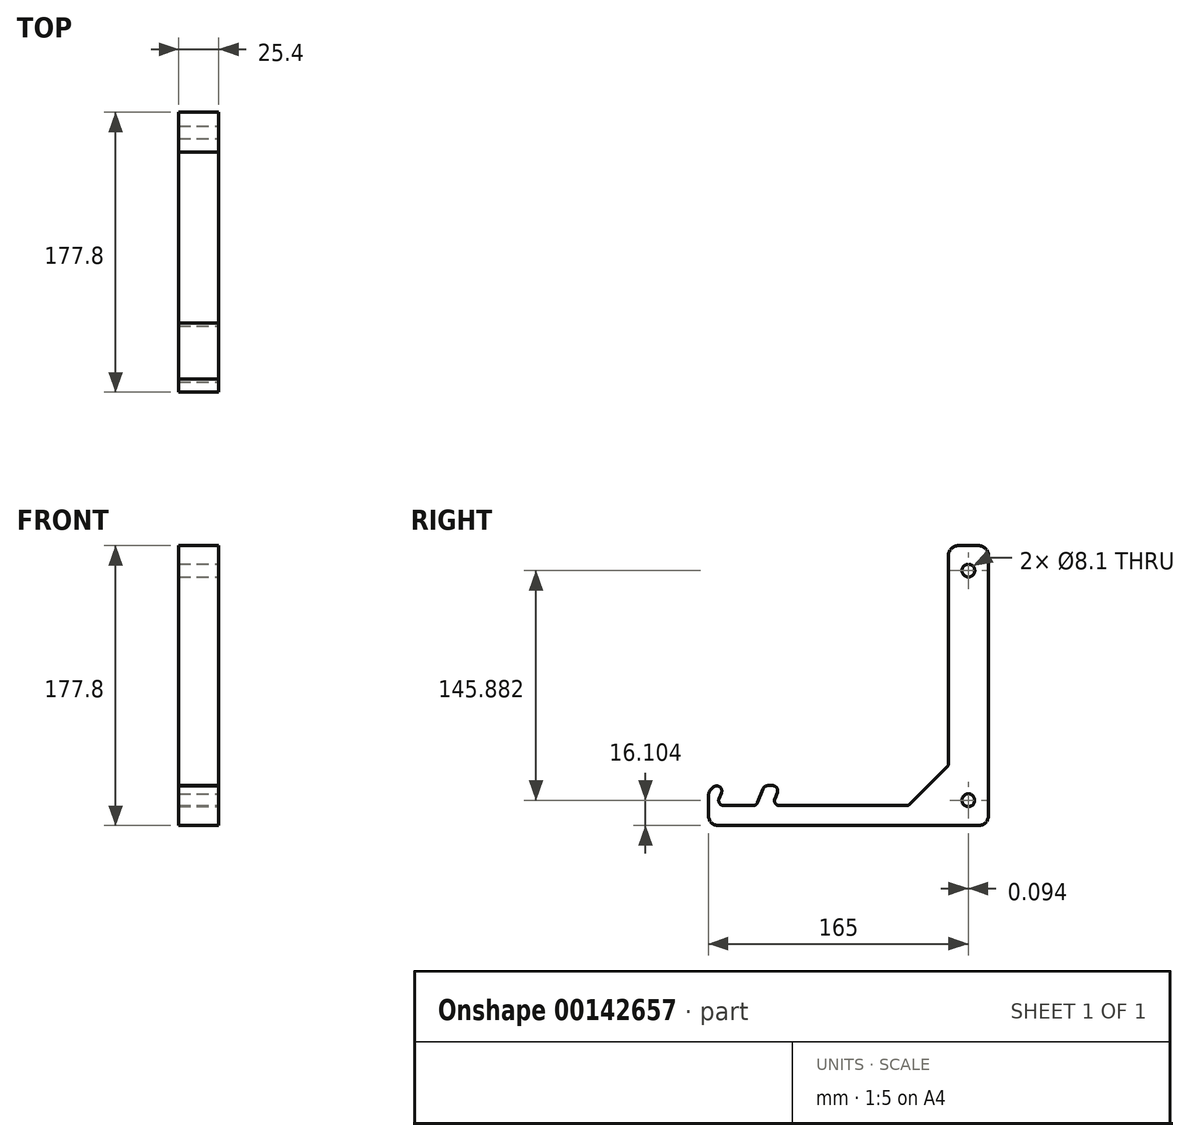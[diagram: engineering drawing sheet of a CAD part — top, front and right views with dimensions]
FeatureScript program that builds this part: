
annotation { "Feature Type Name" : "Feature", "Feature Type Description" : "" }
export const myFeature = defineFeature(function(context is Context, id is Id, definition is map)
    precondition{}
    {
        {
            var Q0;
            Q0=qCreatedBy(makeId("Right.planeOp"),FACE);
            var sketch = newSketch(context, id + "F0", { "sketchPlane" : qUnion([Q0])});
            skLineSegment(sketch, "E0", {"start": v(0, 0) * mm, "end": v(-177.8, 0) * mm});
            skLineSegment(sketch, "E1", {"start": v(-177.8, 0) * mm, "end": v(-177.8, 25.4) * mm});
            skLineSegment(sketch, "E2", {"start": v(-177.8, 25.4) * mm, "end": v(-167.8, 25.4) * mm});
            skLineSegment(sketch, "E3", {"start": v(-167.8, 25.4) * mm, "end": v(-172.8, 12.7) * mm});
            skLineSegment(sketch, "E4", {"start": v(-172.8, 12.7) * mm, "end": v(-147.4, 12.7) * mm});
            skLineSegment(sketch, "E5", {"start": v(-147.4, 12.7) * mm, "end": v(-142.4, 25.4) * mm});
            skLineSegment(sketch, "E6", {"start": v(-142.4, 25.4) * mm, "end": v(-132.4, 25.4) * mm});
            skLineSegment(sketch, "E7", {"start": v(-132.4, 25.4) * mm, "end": v(-137.4, 12.7) * mm});
            skLineSegment(sketch, "E8", {"start": v(-137.4, 12.7) * mm, "end": v(-25.4, 12.7) * mm});
            skLineSegment(sketch, "E9", {"start": v(-25.4, 12.7) * mm, "end": v(-25.4, 177.8) * mm});
            skLineSegment(sketch, "E10", {"start": v(-25.4, 177.8) * mm, "end": v(0, 177.8) * mm});
            skLineSegment(sketch, "E11", {"start": v(0, 177.8) * mm, "end": v(0, 0) * mm});
            skSolve(sketch);
        }
        {
            var Q0;
            Q0 = qSketchRegion(id + "F0", true);
            extrude(context, id + "F1", {"entities" : qUnion([Q0]), "depth" : 25.4 * mm});
        }
        {
            var Q0;
            Q0=makeQuery(id+"F1.opExtrude","SWEPT_EDGE",EDGE,{"disambiguationData":[OSD([sQuery(id+"F0.wireOp",EDGE,"E8"),sQuery(id+"F0.wireOp",EDGE,"E9")])]});
            chamfer(context, id + "F2", {"entities" : qUnion([Q0]), "width" : 25.4 * mm, "tangentPropagation" : true});
        }
        {
            var Q0;
            Q0=makeQuery(id+"F1.opExtrude","SWEPT_EDGE",EDGE,{"disambiguationData":[OSD([sQuery(id+"F0.wireOp",EDGE,"E0"),sQuery(id+"F0.wireOp",EDGE,"E11")])]});
            var Q1;
            Q1=makeQuery(id+"F1.opExtrude","SWEPT_EDGE",EDGE,{"disambiguationData":[OSD([sQuery(id+"F0.wireOp",EDGE,"E10"),sQuery(id+"F0.wireOp",EDGE,"E11")])]});
            var Q2;
            Q2=makeQuery(id+"F1.opExtrude","SWEPT_EDGE",EDGE,{"disambiguationData":[OSD([sQuery(id+"F0.wireOp",EDGE,"E9"),sQuery(id+"F0.wireOp",EDGE,"E10")])]});
            var Q3;
            Q3=makeQuery(id+"F1.opExtrude","SWEPT_EDGE",EDGE,{"disambiguationData":[OSD([sQuery(id+"F0.wireOp",EDGE,"E1"),sQuery(id+"F0.wireOp",EDGE,"E2")])]});
            var Q4;
            Q4=makeQuery(id+"F1.opExtrude","SWEPT_EDGE",EDGE,{"disambiguationData":[OSD([sQuery(id+"F0.wireOp",EDGE,"E0"),sQuery(id+"F0.wireOp",EDGE,"E1")])]});
            fillet(context, id + "F3", {"entities" : qUnion([Q0, Q1, Q2, Q3, Q4]), "radius" : 6.35 * mm, "tangentPropagation" : true, "allowEdgeOverflow" : false});
        }
        {
            var Q0;
            Q0=makeQuery(id+"F1.opExtrude","SWEPT_EDGE",EDGE,{"disambiguationData":[OSD([sQuery(id+"F0.wireOp",EDGE,"E3"),sQuery(id+"F0.wireOp",EDGE,"E4")])]});
            var Q1;
            Q1=makeQuery(id+"F1.opExtrude","SWEPT_EDGE",EDGE,{"disambiguationData":[OSD([sQuery(id+"F0.wireOp",EDGE,"E7"),sQuery(id+"F0.wireOp",EDGE,"E8")])]});
            var Q2;
            Q2=makeQuery(id+"F1.opExtrude","SWEPT_EDGE",EDGE,{"disambiguationData":[OSD([sQuery(id+"F0.wireOp",EDGE,"E4"),sQuery(id+"F0.wireOp",EDGE,"E5")])]});
            var Q3;
            Q3=makeQuery(id+"F1.opExtrude","SWEPT_EDGE",EDGE,{"disambiguationData":[OSD([sQuery(id+"F0.wireOp",EDGE,"E5"),sQuery(id+"F0.wireOp",EDGE,"E6")])]});
            var Q4;
            Q4=makeQuery(id+"F1.opExtrude","SWEPT_EDGE",EDGE,{"disambiguationData":[OSD([sQuery(id+"F0.wireOp",EDGE,"E6"),sQuery(id+"F0.wireOp",EDGE,"E7")])]});
            var Q5;
            Q5=makeQuery(id+"F1.opExtrude","SWEPT_EDGE",EDGE,{"disambiguationData":[OSD([sQuery(id+"F0.wireOp",EDGE,"E2"),sQuery(id+"F0.wireOp",EDGE,"E3")])]});
            var Q6;
            {var subQ0=sQuery(id+"F0.wireOp",EDGE,"E8");Q6=makeQuery(id+"F2.opChamfer","BLEND_EDGE",EDGE,{"blendedFrom":[makeQuery(id+"F1.opExtrude","SWEPT_EDGE",EDGE,{"disambiguationData":[OSD([subQ0,sQuery(id+"F0.wireOp",EDGE,"E9")])]}),makeQuery(id+"F1.opExtrude","SWEPT_FACE",FACE,{"disambiguationData":[OSD([subQ0])]})],"blendedInto":[makeQuery(id+"F1.opExtrude","SWEPT_FACE",FACE,{"disambiguationData":[OSD([subQ0])]})]});}
            var Q7;
            {var subQ0=sQuery(id+"F0.wireOp",EDGE,"E9");Q7=makeQuery(id+"F2.opChamfer","BLEND_EDGE",EDGE,{"blendedFrom":[makeQuery(id+"F1.opExtrude","SWEPT_EDGE",EDGE,{"disambiguationData":[OSD([sQuery(id+"F0.wireOp",EDGE,"E8"),subQ0])]}),makeQuery(id+"F1.opExtrude","SWEPT_FACE",FACE,{"disambiguationData":[OSD([subQ0])]})],"blendedInto":[makeQuery(id+"F1.opExtrude","SWEPT_FACE",FACE,{"disambiguationData":[OSD([subQ0])]})]});}
            fillet(context, id + "F4", {"entities" : qUnion([Q0, Q1, Q2, Q3, Q4, Q5, Q6, Q7]), "radius" : 3.17 * mm, "tangentPropagation" : true, "allowEdgeOverflow" : false});
        }
        {
            var Q0;
            Q0=makeQuery(id+"F1.opExtrude","CAP_FACE",FACE,{"disambiguationData":[OSD([sQuery(id+"F0.wireOp",EDGE,"E0"),sQuery(id+"F0.wireOp",EDGE,"E1"),sQuery(id+"F0.wireOp",EDGE,"E2"),sQuery(id+"F0.wireOp",EDGE,"E3"),sQuery(id+"F0.wireOp",EDGE,"E4"),sQuery(id+"F0.wireOp",EDGE,"E5"),sQuery(id+"F0.wireOp",EDGE,"E6"),sQuery(id+"F0.wireOp",EDGE,"E7"),sQuery(id+"F0.wireOp",EDGE,"E8"),sQuery(id+"F0.wireOp",EDGE,"E9"),sQuery(id+"F0.wireOp",EDGE,"E10"),sQuery(id+"F0.wireOp",EDGE,"E11")])],"isStart":false});
            var sketch = newSketch(context, id + "F5", { "sketchPlane" : qUnion([Q0])});
            skLineSegment(sketch, "E12", {"start": v(-12.7, 177.8) * mm, "end": v(-12.81, 0) * mm, "construction": true});
            skCircle(sketch, "E13", {"center": v(-12.7, 161.99) * mm, "radius": 4.05 * mm});
            skCircle(sketch, "E14", {"center": v(-12.8, 16.1) * mm, "radius": 4.05 * mm});
            skSolve(sketch);
        }
        {
            var Q0;
            Q0 = qSketchRegion(id + "F5", true);
            extrude(context, id + "F6", {"entities" : qUnion([Q0]), "operationType" : NewBodyOperationType.REMOVE, "endBound" : BoundingType.THROUGH_ALL, "oppositeDirection" : true, "depth" : 25.4 * mm});
        }
    });
